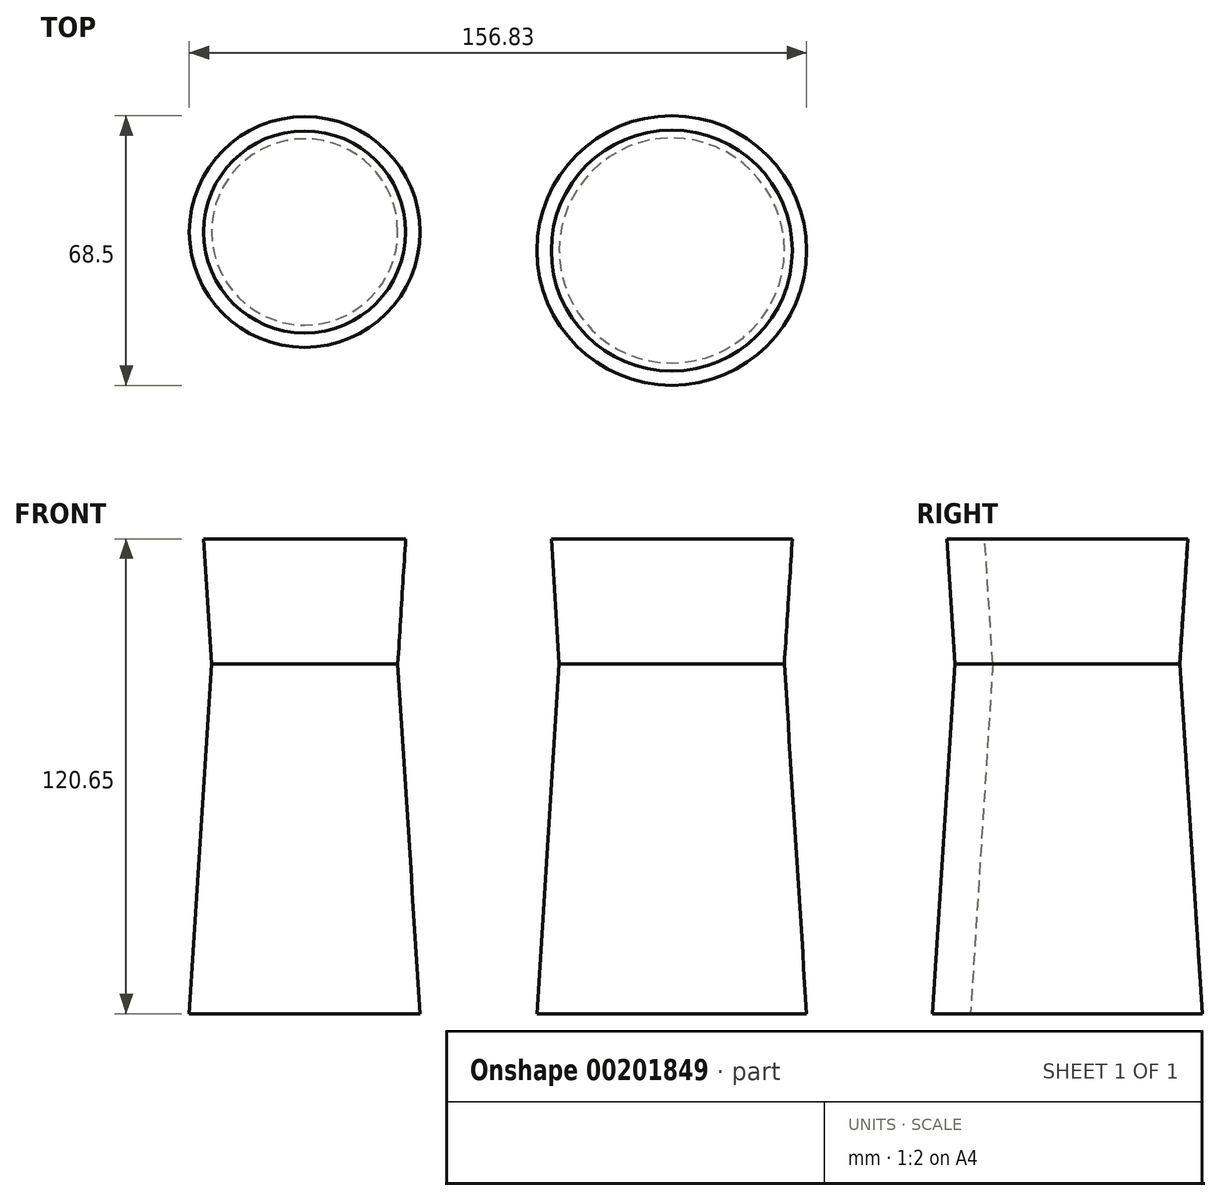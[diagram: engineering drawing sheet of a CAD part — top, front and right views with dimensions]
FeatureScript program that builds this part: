
annotation { "Feature Type Name" : "Feature", "Feature Type Description" : "" }
export const myFeature = defineFeature(function(context is Context, id is Id, definition is map)
    precondition{}
    {
        {
            var Q0;
            Q0=qCreatedBy(makeId("Top.planeOp"),FACE);
            var sketch = newSketch(context, id + "F0", { "sketchPlane" : qUnion([Q0])});
            skLineSegment(sketch, "E0", {"start": v(-61.61, 29.52) * mm, "end": v(43.93, 29.52) * mm});
            skLineSegment(sketch, "E1", {"start": v(43.93, 29.52) * mm, "end": v(-61.61, 29.52) * mm});
            skCircle(sketch, "E2", {"center": v(-62.47, 4.7) * mm, "radius": 23.65 * mm});
            skCircle(sketch, "E3", {"center": v(30.8, 0) * mm, "radius": 28.6 * mm});
            skLineSegment(sketch, "E4", {"start": v(-62.47, 4.7) * mm, "end": v(30.8, 0) * mm});
            skLineSegment(sketch, "E5", {"start": v(-62.47, 4.7) * mm, "end": v(-61.61, 29.52) * mm});
            skLineSegment(sketch, "E6.MirrorCS", {"start": v(40.89, -30.7) * mm, "end": v(-64.11, -20.07) * mm});
            skSolve(sketch);
        }
        {
            var Q0;
            Q0 = qSketchRegion(id + "F0", true);
            extrude(context, id + "F1", {"entities" : qUnion([Q0]), "depth" : 31.75 * mm, "hasDraft" : true, "draftAngle" : 3.64 * degree, "hasSecondDirection" : true, "secondDirectionOppositeDirection" : true, "secondDirectionDepth" : 88.9 * mm, "hasSecondDirectionDraft" : true, "secondDirectionDraftAngle" : 3.64 * degree});
        }
    });
